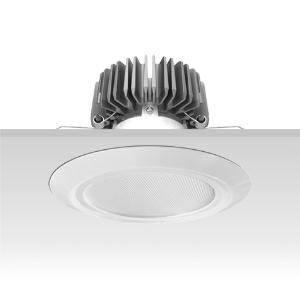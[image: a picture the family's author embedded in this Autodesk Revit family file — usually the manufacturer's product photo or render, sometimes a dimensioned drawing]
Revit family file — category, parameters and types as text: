
# Revit family: 3f_filippi_-_3f_reno_bianco_ampio_3f_filippi_-_30629_a01048_-_3f_reno_200_wh_3000-840_wide___smp_wh_c405
name_source: partatom
category: Lighting Fixtures
units: mm (PartAtom-declared; Revit-internal decimal feet)

## family parameters
Cut with Voids When Loaded = No
Host = Face
Light Source = No
Part Type = Normal
Room Calculation Point = No
Round Connector Dimension = Use Diameter
Shared = No

## types (1)
- 3F Filippi - 3F Reno Bianco Ampio (1 x LED, 2312 lm, 28 W, 4000 K)
    Apparent Load = 28 VA
    Approval mark = CE
    CIE Flux Codes = 74 92 98 100 100
    Color Rendering = 80
    Color Temperature = 4000 K
    Control Gear = Electronic ballast
    Default Elevation = 1800 mm
    Description = ILLUMINOTECHNICAL
Luminous efficiency 100% (DLOR 100%, ULOR 0%).
Initial luminous flux of the luminaire 2312 lm.
Direct symmetric wide distribution.
Installation Interdistance Transv.D = 1.06 x hu - Long.D = 1.04 x hu.
Tabular UGR (CIE 117 - 4H-8H; S=0.25H; 70/50/20): RUG 22.5 - 22.3.
Beam angle: 70° - 69°.
Luminous efficacy 83 lm/W.
Lifetime (L90/B10): 30000 h. (tq+25°C)
Lifetime (L85/B10): 50000 h. (tq+25°C)
Lifetime (L70/B10): 80000 h. (tq+25°C)
Sudden decreased luminous flux after 50000 hours: 0% (C0).
Photobiological safety in compliance with IEC/TR 62778: RG0 risk exempt, (IEC 62471).
In compliance with IEC/EN 62722-2-1 - IEC/EN 62717 standards.

SOURCE
Compact LED module 3000/840.
Energy efficiency class (UE 2019/2020 - UE 2019/2015): D.
CIE 13.3 Colour rendering index: CRI >80 (R9 <50%).
IES TM-30 Fidelity Index: Rf = 84 Rg = 95.
CCT nominal colour temperature 4000 K.
Colour initial tolerance (MacAdam): SDCM 3.
Zhaga Book 3 compliant.

MECHANICAL
Passive heat dissipator in die-casting aluminium, oversized, for optimum thermal management of the LED module.
Parabolic element with graduated/concentric rings in white polycarbonate.
Transparent external lens with glossy and satin differentiated surfaces, with a cooling and anti-insect system in methacrylate (PMMA).
Fastening spring clips in stainless steel.
Dimensions: diameter 226 mm, height 146 mm. Weight 1.63 kg.
IP44 protection degree for exposed part, IP20 for recessed part.
Mechanical strength to impacts IK05 (0.7 joule).
Glow-wire test resistance 650°C.

ELECTRICAL
Wiring on a separate unit.
Halogen Free electronic wiring 230V-50/60Hz, power factor 0.95, THD <25%, constant output current, SELV, class II, 1 driver.
Power of the luminaire 28 W.
ENEC - CE.
SAFE FLICKER: PstLM=<1 and SVM=<0.4 (IEC TR 61547-1 and IEC TR 63158), to ensure a more comfortable and safe light.
Luminaire compliant with EN 60598-2-22 for power supply from a centralised emergency system CPSS (Central Power Supply System), not incorporated in the luminaire - high risk areas excluded. The default power and flux are 100% in AC and 100% in DC.
Ambient temperature from 0°C to +25°C.
Temperature class T6 max 85°C.
Relative humidity UR: <85%.

INSTALLATION
Pull-up recessed fitting.
False ceiling carving: 200 mm.
All accessories dedicated to this product are available on the Catalog and on our website www.3F-Filippi.com.

ACCESSORIES
A01048 - Anti-glare microprismatic SMP diffuser in methacrylate (PMMA), locked and in line with the trim, in white polycarbonate.

APPLICATIONS
Suitable product for food production plants (HACCP), IFS (Food Version 6), BRC (GSFS Food Version 7).
Environments: architectural, commercial, exhibition areas, transit areas, corridors, shops, display windows, service areas.
In false ceilings with narrow voids.

WARNING
Luminaire designed for disposal/recycling at end-of-life.
Replaceable (LED only) light source by a professional. Replaceable control gear by a professional.
    Height = 0 mm  [stored 0 ft]
    Lamp = 1 x LED
    Lamp Light Flux = 2312 lm
    Lamp Power = 28 W
    Lamp count = 1
    Length = 226 mm
    Lifetime = 50000 h
    Luminous efficacy = 83 lm/W
    Manufacturer = 3F Filippi
    ModVariant = No
    Model = 3F Filippi - 30629+A01048 - 3F Reno 200 WH 3000-840 WIDE + SMP WH
    Mounting Place = Ceiling
    Mounting Type = Recessed
    Number of Poles = 1
    OnlyDefault = Yes
    Power Factor = 1
    Product Name = 3F Filippi - 3F Reno Bianco Ampio
    Product group = recessed luminaire
    ProductGroupID = 4
    Protection Class = Protection class II
    Protection Degree = IP 20
    RLX_Detail_Level = 1
    RLX_Emergency_Light_Flux = 0 lm
    RLX_Emergency_Type = 0
    RLX_Emergency_Type_DB = No
    RlxData = <blob elided: 94085 chars, md5=21d5ac9c>
    Socket = socket
    Standby Power = 0 W
    System Light Flux = 2312 lm
    System Power = 28 W
    Type Comments = Product without accessories
    Type Image = 3ffilippi_3f_reno_200_wh_vs_smp.jpg
    URL = http://relux.com
    VarID = ---
    Voltage = 0 V
    Weight = 0.00 kg
    Width = 0 mm  [stored 0 ft]

note: [stored X ft] marks values corroborated as IEEE doubles in the binary element streams (Revit-internal decimal feet)

## geometry (parser evidence)
native form markers: Blend x4, Sweep x10
no freeform markers — native parametric forms only
